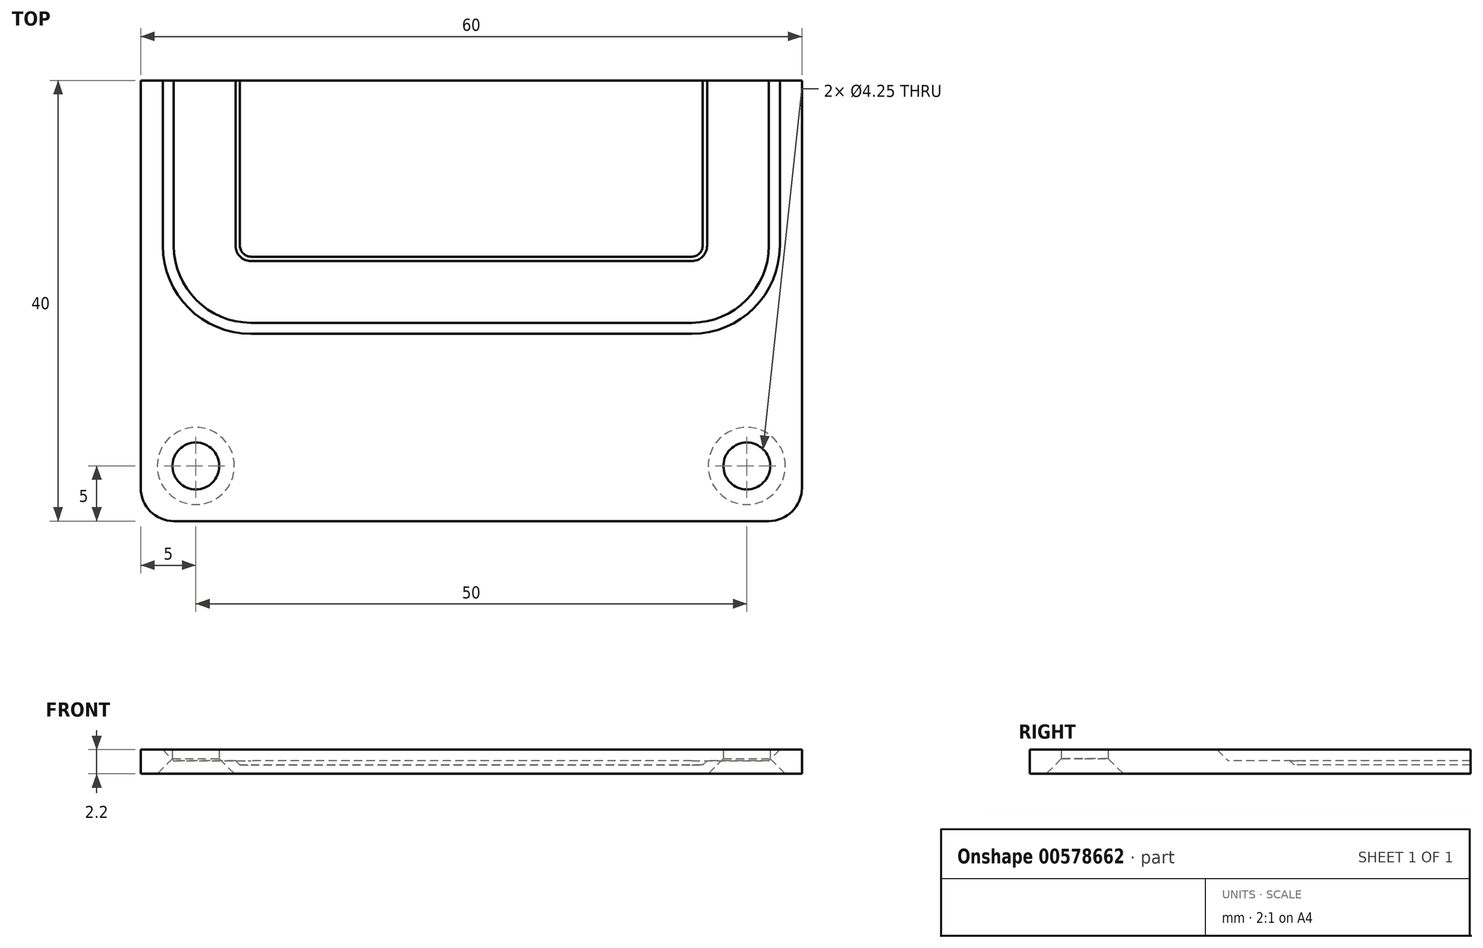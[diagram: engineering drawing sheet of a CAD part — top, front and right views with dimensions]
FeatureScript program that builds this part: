
annotation { "Feature Type Name" : "Feature", "Feature Type Description" : "" }
export const myFeature = defineFeature(function(context is Context, id is Id, definition is map)
    precondition{}
    {
        {
            var Q0;
            Q0=qCreatedBy(makeId("Top.planeOp"),FACE);
            var sketch = newSketch(context, id + "F0", { "sketchPlane" : qUnion([Q0])});
            skLineSegment(sketch, "E0.bottom", {"start": v(30, -20) * mm, "end": v(-30, -20) * mm});
            skLineSegment(sketch, "E0.top", {"start": v(30, 20) * mm, "end": v(-30, 20) * mm});
            skLineSegment(sketch, "E0.left", {"start": v(30, -20) * mm, "end": v(30, 20) * mm});
            skLineSegment(sketch, "E0.right", {"start": v(-30, -20) * mm, "end": v(-30, 20) * mm});
            skPoint(sketch, "E0.middle", {"position": v(0, 0) * mm});
            skPoint(sketch, "E1", {"position": v(-25, -15) * mm});
            skPoint(sketch, "E2", {"position": v(25, -15) * mm});
            skSolve(sketch);
        }
        {
            var Q0;
            Q0=makeQuery(id+"F0.imprint","IMPRINT",FACE,{"disambiguationData":[TD([[makeQuery(id+"F0.imprint","IMPRINT",EDGE,{"derivedFrom":sQuery(id+"F0.wireOp",EDGE,"E0.bottom")}),-1.0]])]});
            extrude(context, id + "F1", {"entities" : qUnion([Q0]), "depth" : 2.2 * mm, "offsetDistance" : 25 * mm});
        }
        {
            var Q0;
            Q0=sQuery(id+"F0.wireOp",VERTEX,"E1");
            var Q1;
            Q1=sQuery(id+"F0.wireOp",VERTEX,"E2");
            var Q2;
            Q2=makeQuery(id+"F1.opExtrude","SWEPT_BODY",BODY,{"disambiguationData":[OSD([sQuery(id+"F0.wireOp",EDGE,"E0.bottom"),sQuery(id+"F0.wireOp",EDGE,"E0.top"),sQuery(id+"F0.wireOp",EDGE,"E0.left"),sQuery(id+"F0.wireOp",EDGE,"E0.right")])]});
            hole(context, id + "F2", {"style" : HoleStyle.C_SINK, "endStyle" : HoleEndStyle.BLIND, "oppositeDirection" : true, "holeDiameter" : 4.25 * mm, "cSinkDiameter" : 7 * mm, "cSinkAngle" : 90 * degree, "majorDiameter" : 5 * mm, "holeDepth" : 15 * mm, "isTappedThrough" : true, "tappedDepth" : 12 * mm, "tapClearance" : 3, "locations" : qUnion([Q0, Q1]), "scope" : qUnion([Q2])});
        }
        {
            var Q0;
            Q0=makeQuery(id+"F1.opExtrude","SWEPT_EDGE",EDGE,{"disambiguationData":[OSD([sQuery(id+"F0.wireOp",EDGE,"E0.bottom"),sQuery(id+"F0.wireOp",EDGE,"E0.right")])]});
            var Q1;
            Q1=makeQuery(id+"F1.opExtrude","SWEPT_EDGE",EDGE,{"disambiguationData":[OSD([sQuery(id+"F0.wireOp",EDGE,"E0.bottom"),sQuery(id+"F0.wireOp",EDGE,"E0.left")])]});
            fillet(context, id + "F3", {"entities" : qUnion([Q0, Q1]), "radius" : 3 * mm, "tangentPropagation" : true, "allowEdgeOverflow" : false});
        }
        {
            var Q0;
            Q0=makeQuery(id+"F1.opExtrude","CAP_FACE",FACE,{"disambiguationData":[OSD([sQuery(id+"F0.wireOp",EDGE,"E0.bottom"),sQuery(id+"F0.wireOp",EDGE,"E0.top"),sQuery(id+"F0.wireOp",EDGE,"E0.left"),sQuery(id+"F0.wireOp",EDGE,"E0.right")])],"isStart":false});
            var sketch = newSketch(context, id + "F4", { "sketchPlane" : qUnion([Q0])});
            skLineSegment(sketch, "E3.bottom", {"start": v(-25, 20) * mm, "end": v(25, 20) * mm});
            skLineSegment(sketch, "E3.top", {"start": v(-25, 0) * mm, "end": v(25, 0) * mm});
            skLineSegment(sketch, "E3.left", {"start": v(-25, 20) * mm, "end": v(-25, 0) * mm});
            skLineSegment(sketch, "E3.right", {"start": v(25, 20) * mm, "end": v(25, 0) * mm});
            skSolve(sketch);
        }
        {
            var Q0;
            Q0=makeQuery(id+"F4.imprint","IMPRINT",FACE,{"disambiguationData":[TD([[makeQuery(id+"F4.imprint","IMPRINT",EDGE,{"derivedFrom":sQuery(id+"F4.wireOp",EDGE,"E3.bottom")}),1.0]])]});
            extrude(context, id + "F5", {"entities" : qUnion([Q0]), "operationType" : NewBodyOperationType.REMOVE, "oppositeDirection" : true, "depth" : 1 * mm, "offsetDistance" : 25 * mm});
        }
        {
            var Q0;
            Q0=makeQuery(id+"F5.boolean.opBoolean","COPY",EDGE,{"derivedFrom":makeQuery(id+"F5.opExtrude","SWEPT_EDGE",EDGE,{"disambiguationData":[OSD([sQuery(id+"F4.wireOp",EDGE,"E3.top"),sQuery(id+"F4.wireOp",EDGE,"E3.right")])]})});
            var Q1;
            Q1=makeQuery(id+"F5.boolean.opBoolean","COPY",EDGE,{"derivedFrom":makeQuery(id+"F5.opExtrude","SWEPT_EDGE",EDGE,{"disambiguationData":[OSD([sQuery(id+"F4.wireOp",EDGE,"E3.top"),sQuery(id+"F4.wireOp",EDGE,"E3.left")])]})});
            fillet(context, id + "F6", {"entities" : qUnion([Q0, Q1]), "radius" : 5 * mm, "tangentPropagation" : true, "allowEdgeOverflow" : false});
        }
        {
            var Q0;
            Q0=makeQuery(id+"F6.opFillet","BLEND_EDGE",EDGE,{"blendedFrom":[makeQuery(id+"F5.boolean.opBoolean","COPY",EDGE,{"derivedFrom":makeQuery(id+"F5.opExtrude","SWEPT_EDGE",EDGE,{"disambiguationData":[OSD([sQuery(id+"F4.wireOp",EDGE,"E3.top"),sQuery(id+"F4.wireOp",EDGE,"E3.right")])]})}),makeQuery(id+"F1.opExtrude","CAP_FACE",FACE,{"disambiguationData":[OSD([sQuery(id+"F0.wireOp",EDGE,"E0.bottom"),sQuery(id+"F0.wireOp",EDGE,"E0.top"),sQuery(id+"F0.wireOp",EDGE,"E0.left"),sQuery(id+"F0.wireOp",EDGE,"E0.right")])],"isStart":false})],"blendedInto":[makeQuery(id+"F1.opExtrude","CAP_FACE",FACE,{"disambiguationData":[OSD([sQuery(id+"F0.wireOp",EDGE,"E0.bottom"),sQuery(id+"F0.wireOp",EDGE,"E0.top"),sQuery(id+"F0.wireOp",EDGE,"E0.left"),sQuery(id+"F0.wireOp",EDGE,"E0.right")])],"isStart":false})]});
            chamfer(context, id + "F7", {"entities" : qUnion([Q0]), "width" : 3 * mm, "tangentPropagation" : true});
        }
        {
            var Q0;
            Q0=makeQuery(id+"F5.boolean.opBoolean","COPY",FACE,{"derivedFrom":makeQuery(id+"F5.opExtrude","CAP_FACE",FACE,{"disambiguationData":[OSD([sQuery(id+"F4.wireOp",EDGE,"E3.bottom"),sQuery(id+"F4.wireOp",EDGE,"E3.top"),sQuery(id+"F4.wireOp",EDGE,"E3.left"),sQuery(id+"F4.wireOp",EDGE,"E3.right")])],"isStart":false})});
            var sketch = newSketch(context, id + "F8", { "sketchPlane" : qUnion([Q0])});
            skLineSegment(sketch, "E4.0", {"start": v(22, 5) * mm, "end": v(22, 20) * mm});
            skLineSegment(sketch, "E4.1", {"start": v(-22, 20) * mm, "end": v(-22, 5) * mm});
            skArc(sketch, "E4.2", {"start": v(-22, 5) * mm, "mid": v(-21.41, 3.59) * mm, "end": v(-20, 3) * mm});
            skLineSegment(sketch, "E4.3", {"start": v(-20, 3) * mm, "end": v(20, 3) * mm});
            skArc(sketch, "E4.4", {"start": v(20, 3) * mm, "mid": v(21.41, 3.59) * mm, "end": v(22, 5) * mm});
            skSolve(sketch);
        }
        {
            var Q0;
            {var subQ1=sQuery(id+"F8.wireOp",EDGE,"E4.0");Q0=makeQuery(id+"F8.imprint","IMPRINT",FACE,{"disambiguationData":[TD([[makeQuery(id+"F8.imprint","IMPRINT",EDGE,{"derivedFrom":subQ1}),1.0]])]});}
            extrude(context, id + "F9", {"entities" : qUnion([Q0]), "operationType" : NewBodyOperationType.REMOVE, "oppositeDirection" : true, "depth" : .4 * mm, "offsetDistance" : 25 * mm});
        }
        {
            var Q0;
            Q0=makeQuery(id+"F9.boolean.opBoolean","COPY",EDGE,{"derivedFrom":makeQuery(id+"F9.opExtrude","CAP_EDGE",EDGE,{"disambiguationData":[OSD([sQuery(id+"F8.wireOp",EDGE,"E4.4")])],"isStart":false})});
            chamfer(context, id + "F10", {"entities" : qUnion([Q0]), "width" : 1 * mm, "tangentPropagation" : true});
        }
    });
